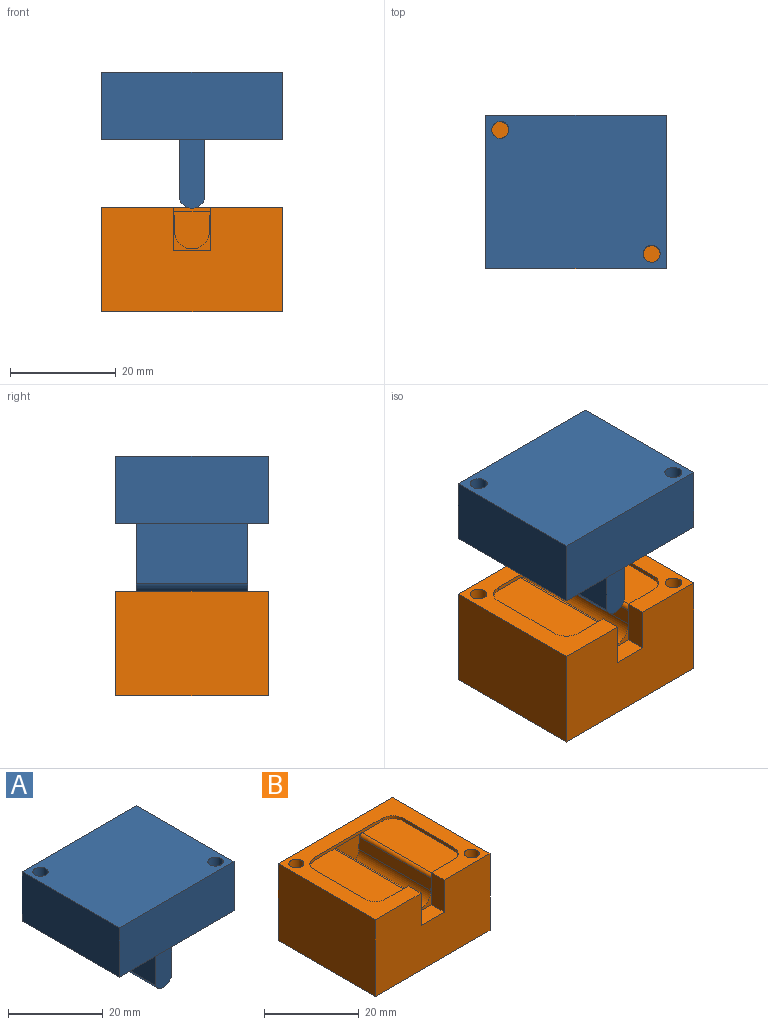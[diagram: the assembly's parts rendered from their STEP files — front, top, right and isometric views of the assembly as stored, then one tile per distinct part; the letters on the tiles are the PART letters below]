
ASSEMBLY  parts=2 mates=2
PART A: 13 faces, bbox 34.2x29x25.8 mm
  f0: plane 34.16x12.7mm, normal (0,1,0), area 433.9mm2, adj f1,f3,f4,f5
  f1: plane 28.96x12.7mm, normal (-1,0,0), area 367.7mm2, adj f0,f2,f4,f5
  f2: plane 34.16x12.7mm, normal (0,-1,0), area 433.9mm2, adj f1,f3,f4,f5
  f3: plane 28.96x12.7mm, normal (1,0,0), area 367.7mm2, adj f0,f2,f4,f5
  f4: plane 34.16x28.96mm, normal (0,0,1), area 972.9mm2, adj f0,f1,f2,f3,f11,f12
  f5: plane 34.16x28.96mm, normal (0,0,-1), area 872mm2, adj f0,f1,f2,f3,f6,f7,f9,f10
  f6: plane 21.13x11.43mm, normal (1,0,0), area 241.5mm2, adj f5,f8,f9,f10
  f7: plane 21.13x11.43mm, normal (-1,0,0), area 241.5mm2, adj f5,f8,f9,f10
  f8: cylinder r=2.54mm len=21.13mm, axis (0,1,0), area 131.3mm2, adj f6,f7,f9,f10
  f9: plane 13.1x4.78mm, normal (0,-1,0), area 60.4mm2, adj f5,f6,f7,f8
  f10: plane 13.1x4.78mm, normal (0,1,0), area 60.4mm2, adj f5,f6,f7,f8
  f11: cylinder r=1.61mm len=12.7mm, axis (0,0,-1), area 128.7mm2, adj f4,f5
  f12: cylinder r=1.61mm len=12.7mm, axis (0,0,-1), area 128.7mm2, adj f4,f5
PART B: 32 faces, bbox 34.2x29x19.8 mm
  f0: plane 6.67x1.33mm, normal (0,1,0), area 5.2mm2, adj f4,f10,f17,f26,f30
  f1: plane 21.46x3.81mm, normal (1,0,0.03), area 66.1mm2, adj f2,f15,f20,f21,f27,f28
  f2: cylinder r=3.3mm len=21.46mm, axis (0,-1,0), area 222.6mm2, adj f1,f3,f21,f28
  f3: plane 21.46x3.81mm, normal (-1,0,0.03), area 66.1mm2, adj f2,f15,f20,f21,f26,f28
  f4: plane 21.34x9.11mm, normal (0,0,1), area 189.9mm2, adj f0,f8,f9,f10,f15,f26
  f5: plane 34.16x19.81mm, normal (0,1,0), area 676.8mm2, adj f6,f16,f17,f19
  f6: plane 28.96x19.81mm, normal (-1,0,0), area 573.7mm2, adj f5,f7,f17,f19
  f7: plane 34.16x19.81mm, normal (0,-1,0), area 620.2mm2, adj f6,f16,f17,f19,f29,f30,f31
  f8: cylinder r=3.17mm len=3.18mm, axis (0,0,-1), area 3.8mm2, adj f4,f9,f15,f17
  f9: plane 14.99x0.76mm, normal (-1,0,0), area 11.4mm2, adj f4,f8,f10,f17
  f10: cylinder r=3.17mm len=3.18mm, axis (0,0,-1), area 3.8mm2, adj f0,f4,f9,f17
  f11: plane 6.67x1.33mm, normal (0,1,0), area 5.2mm2, adj f12,f17,f18,f27,f29
  f12: cylinder r=3.17mm len=3.18mm, axis (0,0,-1), area 3.8mm2, adj f11,f13,f17,f18
  f13: plane 14.99x0.76mm, normal (1,0,0), area 11.4mm2, adj f12,f14,f17,f18
  f14: cylinder r=3.17mm len=3.18mm, axis (0,0,-1), area 3.8mm2, adj f13,f15,f17,f18
  f15: plane 20.19x1.5mm, normal (0,-1,0), area 15.6mm2, adj f1,f3,f4,f8,f14,f17,f18,f20
  f16: plane 28.96x19.81mm, normal (1,0,0), area 573.7mm2, adj f5,f7,f17,f19
  f17: plane 34.16x28.96mm, normal (0,0,1), area 389.6mm2, adj f0,f5,f6,f7,f8,f9,f10,f11
  f18: plane 21.34x9.11mm, normal (0,0,1), area 189.9mm2, adj f11,f12,f13,f14,f15,f27
  f19: plane 34.16x28.96mm, normal (0,0,-1), area 989.2mm2, adj f5,f6,f7,f16
  f20: plane 6.86x0.13mm, normal (0,0,-1), area 0.9mm2, adj f1,f3,f15,f21
  f21: plane 7.11x6.86mm, normal (0,-1,0), area 42.8mm2, adj f1,f2,f3,f20
  f22: cylinder r=1.59mm len=6.35mm, axis (0,0,1), area 63.3mm2, adj f17,f23
  f23: plane 3.18x3.18mm, normal (0,0,1), area 7.9mm2, adj f22
  f24: cylinder r=1.59mm len=6.35mm, axis (0,0,1), area 63.3mm2, adj f17,f25
  f25: plane 3.18x3.18mm, normal (0,0,1), area 7.9mm2, adj f24
  f26: cylinder r=0.76mm len=21.34mm, axis (0,1,0), area 25mm2, adj f0,f3,f4,f15,f28
  f27: cylinder r=0.76mm len=21.34mm, axis (0,1,0), area 25mm2, adj f1,f11,f15,f18,f28
  f28: plane 6.92x6.86mm, normal (0,-1,0), area 8.6mm2, adj f1,f2,f3,f26,f27,f29,f30,f31
  f29: plane 8.26x3.81mm, normal (1,0,0), area 31.5mm2, adj f7,f11,f17,f28,f31
  f30: plane 8.26x3.81mm, normal (-1,0,0), area 31.5mm2, adj f0,f7,f17,f28,f31
  f31: plane 6.86x3.81mm, normal (0,0,1), area 26.1mm2, adj f7,f28,f29,f30
PLACE A rot(axis=(0.34,0.66,0.67),0deg) t=(-36.9,-34.81,-17.46)mm
PLACE B rot(axis=(0.34,0.66,0.67),0deg) t=(-36.9,-34.81,-31.11)mm
MATE planar A.f0 <-> B.f5  axis (0,1,0) through (-19.82,-20.33,-11.11)mm
MATE planar B.f16 <-> A.f3  axis (1,0,0) through (-19.82,-34.81,-40.26)mm
